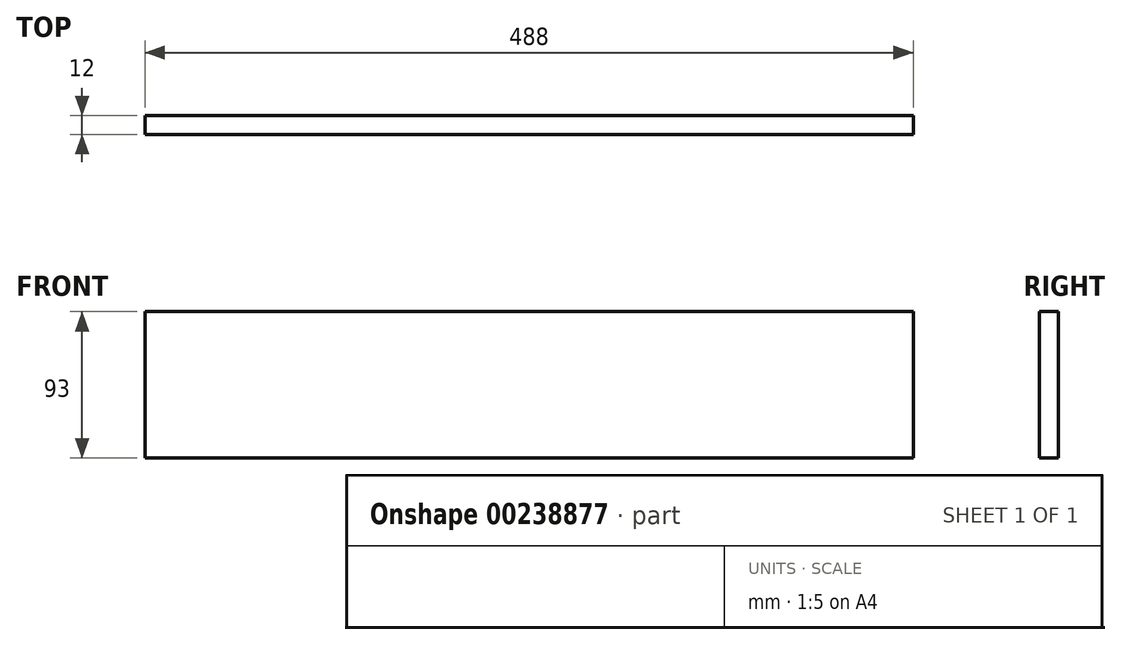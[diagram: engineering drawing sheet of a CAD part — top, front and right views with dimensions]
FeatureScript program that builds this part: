
annotation { "Feature Type Name" : "Feature", "Feature Type Description" : "" }
export const myFeature = defineFeature(function(context is Context, id is Id, definition is map)
    precondition{}
    {
        {
            var Q0;
            Q0=qCreatedBy(makeId("Front.planeOp"),FACE);
            var sketch = newSketch(context, id + "F0", { "sketchPlane" : qUnion([Q0])});
            skLineSegment(sketch, "E0.bottom", {"start": v(0, 0) * mm, "end": v(488, 0) * mm});
            skLineSegment(sketch, "E0.top", {"start": v(0, 93) * mm, "end": v(488, 93) * mm});
            skLineSegment(sketch, "E0.left", {"start": v(0, 0) * mm, "end": v(0, 93) * mm});
            skLineSegment(sketch, "E0.right", {"start": v(488, 0) * mm, "end": v(488, 93) * mm});
            skSolve(sketch);
        }
        {
            var Q0;
            Q0 = qSketchRegion(id + "F0", true);
            extrude(context, id + "F1", {"entities" : qUnion([Q0]), "offsetDistance" : 25 * mm, "depth" : 12 * mm});
        }
    });
